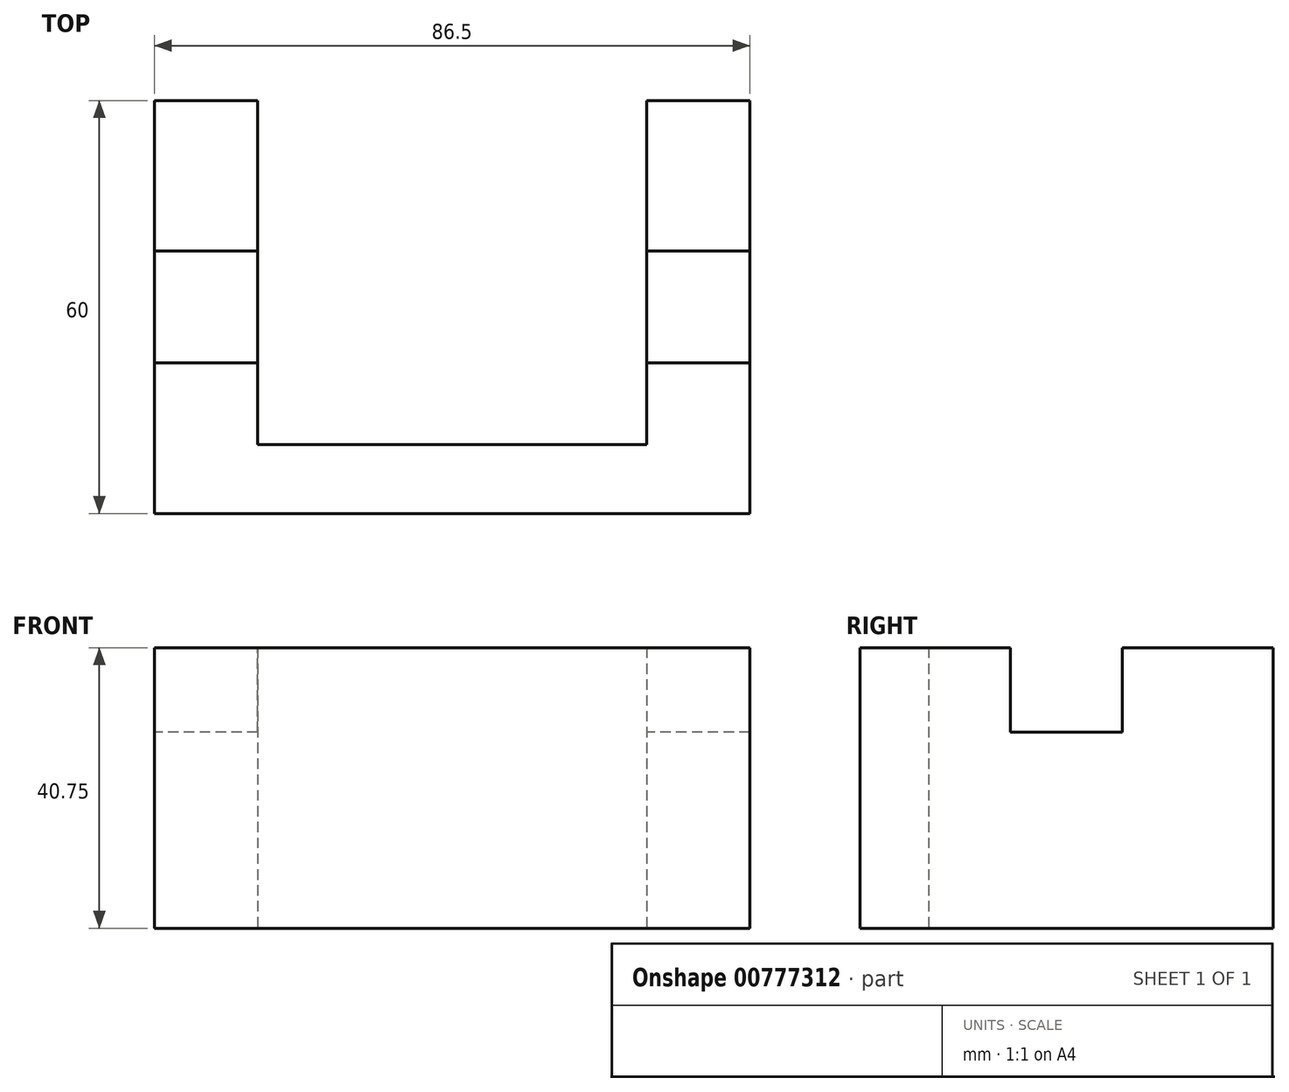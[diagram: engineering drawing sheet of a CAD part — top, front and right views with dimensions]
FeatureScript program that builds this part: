
annotation { "Feature Type Name" : "Feature", "Feature Type Description" : "" }
export const myFeature = defineFeature(function(context is Context, id is Id, definition is map)
    precondition{}
    {
        {
            var Q0;
            Q0=qCreatedBy(makeId("Top.planeOp"),FACE);
            var sketch = newSketch(context, id + "F0", { "sketchPlane" : qUnion([Q0])});
            skLineSegment(sketch, "E0.bottom", {"start": v(7.5, 30) * mm, "end": v(-7.5, 30) * mm});
            skLineSegment(sketch, "E0.top", {"start": v(7.5, -30) * mm, "end": v(-7.5, -30) * mm});
            skLineSegment(sketch, "E0.left", {"start": v(7.5, 30) * mm, "end": v(7.5, -30) * mm});
            skLineSegment(sketch, "E0.right", {"start": v(-7.5, 30) * mm, "end": v(-7.5, -30) * mm});
            skPoint(sketch, "E0.middle", {"position": v(0, 0) * mm});
            skSolve(sketch);
        }
        {
            var Q0;
            Q0 = qSketchRegion(id + "F0", true);
            extrude(context, id + "F1", {"entities" : qUnion([Q0]), "depth" : 28.5 * mm, "offsetDistance" : 25 * mm});
        }
        {
            var Q0;
            Q0=makeQuery(id+"F1.opExtrude","CAP_FACE",FACE,{"disambiguationData":[OSD([sQuery(id+"F0.wireOp",EDGE,"E0.bottom"),sQuery(id+"F0.wireOp",EDGE,"E0.top"),sQuery(id+"F0.wireOp",EDGE,"E0.left"),sQuery(id+"F0.wireOp",EDGE,"E0.right")])],"isStart":false});
            var sketch = newSketch(context, id + "F2", { "sketchPlane" : qUnion([Q0])});
            skLineSegment(sketch, "E1.bottom", {"start": v(7.5, 8.12) * mm, "end": v(-7.5, 8.12) * mm});
            skLineSegment(sketch, "E1.top", {"start": v(7.5, -8.12) * mm, "end": v(-7.5, -8.12) * mm});
            skLineSegment(sketch, "E1.left", {"start": v(7.5, 8.12) * mm, "end": v(7.5, -8.12) * mm});
            skLineSegment(sketch, "E1.right", {"start": v(-7.5, 8.12) * mm, "end": v(-7.5, -8.12) * mm});
            skPoint(sketch, "E1.middle", {"position": v(0, 0) * mm});
            skSolve(sketch);
        }
        {
            var Q0;
            {var subQ0=sQuery(id+"F0.wireOp",EDGE,"E0.left");Q0=makeQuery(id+"F411Q4QD505CHMR_1.boolean.opBoolean","MERGE",FACE,{"derivedFrom":[makeQuery(id+"F1.opExtrude","CAP_FACE",FACE,{"disambiguationData":[OSD([sQuery(id+"F0.wireOp",EDGE,"E0.bottom"),sQuery(id+"F0.wireOp",EDGE,"E0.top"),subQ0,sQuery(id+"F0.wireOp",EDGE,"E0.right")])],"isStart":true}),makeQuery(id+"F411Q4QD505CHMR_1.opExtrude","SWEPT_FACE",FACE,{"disambiguationData":[OSD([subQ0]),TDD([makeQuery(id+"F1.opExtrude","CAP_EDGE",EDGE,{"disambiguationData":[OSD([subQ0])],"isStart":true})])]})]});}
            var sketch = newSketch(context, id + "F3", { "sketchPlane" : qUnion([Q0])});
            skLineSegment(sketch, "E2.bottom", {"start": v(7.5, 20) * mm, "end": v(64, 20) * mm});
            skLineSegment(sketch, "E2.top", {"start": v(7.5, -30) * mm, "end": v(64, -30) * mm});
            skLineSegment(sketch, "E2.left", {"start": v(7.5, 20) * mm, "end": v(7.5, -30) * mm});
            skLineSegment(sketch, "E2.right", {"start": v(64, 20) * mm, "end": v(64, -30) * mm});
            skSolve(sketch);
        }
        {
            var Q0;
            Q0=makeQuery(id+"F3.imprint","IMPRINT",FACE,{"disambiguationData":[TD([[makeQuery(id+"F3.imprint","IMPRINT",EDGE,{"derivedFrom":sQuery(id+"F3.wireOp",EDGE,"E2.bottom")}),-1.0]])]});
            extrude(context, id + "F4", {"entities" : qUnion([Q0]), "operationType" : NewBodyOperationType.REMOVE, "endBound" : BoundingType.THROUGH_ALL, "oppositeDirection" : true, "depth" : 25 * mm, "offsetDistance" : 25 * mm});
        }
        {
            var Q0;
            {var subQ0=sQuery(id+"F2.wireOp",EDGE,"E1.bottom");Q0=makeQuery(id+"F2.imprint","IMPRINT",FACE,{"disambiguationData":[TD([[makeQuery(id+"F2.imprint","IMPRINT",EDGE,{"derivedFrom":subQ0}),-1.0]])]});}
            var Q1;
            {var subQ0=sQuery(id+"F2.wireOp",EDGE,"E1.top");Q1=makeQuery(id+"F2.imprint","IMPRINT",FACE,{"disambiguationData":[TD([[makeQuery(id+"F2.imprint","IMPRINT",EDGE,{"derivedFrom":subQ0}),1.0]])]});}
            extrude(context, id + "F5", {"entities" : qUnion([Q0, Q1]), "operationType" : NewBodyOperationType.ADD, "depth" : 12.25 * mm, "offsetDistance" : 25 * mm});
        }
        {
            var Q0;
            {var subQ0=sQuery(id+"F0.wireOp",EDGE,"E0.left");var subQ1=makeQuery(id+"F1.opExtrude","CAP_EDGE",EDGE,{"disambiguationData":[OSD([subQ0])],"isStart":false});Q0=makeQuery(id+"F5.boolean.opBoolean","MERGE",FACE,{"derivedFrom":[makeQuery(id+"F1.opExtrude","SWEPT_FACE",FACE,{"disambiguationData":[OSD([subQ0])]}),makeQuery(id+"F5.opExtrude","SWEPT_FACE",FACE,{"disambiguationData":[OSD([subQ0]),TDD([makeQuery(id+"F2.imprint","IMPRINT",EDGE,{"disambiguationData":[TD([[makeQuery(id+"F2.imprint","INTERSECT",VERTEX,{"derivedFrom":[makeQuery(id+"F1.opExtrude","CAP_EDGE",EDGE,{"disambiguationData":[OSD([sQuery(id+"F0.wireOp",EDGE,"E0.bottom")])],"isStart":false}),subQ1]}),-1.0]])],"derivedFrom":subQ1})])]}),makeQuery(id+"F5.opExtrude","SWEPT_FACE",FACE,{"disambiguationData":[OSD([subQ0]),TDD([makeQuery(id+"F2.imprint","IMPRINT",EDGE,{"disambiguationData":[TD([[makeQuery(id+"F2.imprint","INTERSECT",VERTEX,{"derivedFrom":[makeQuery(id+"F1.opExtrude","CAP_EDGE",EDGE,{"disambiguationData":[OSD([sQuery(id+"F0.wireOp",EDGE,"E0.top")])],"isStart":false}),subQ1]}),1.0]])],"derivedFrom":subQ1})])]})]});}
            extrude(context, id + "F6", {"entities" : qUnion([Q0]), "operationType" : NewBodyOperationType.ADD, "depth" : 71.5 * mm, "offsetDistance" : 25 * mm});
        }
        {
            var Q0;
            Q0 = qSketchRegion(id + "F3", true);
            extrude(context, id + "F7", {"entities" : qUnion([Q0]), "operationType" : NewBodyOperationType.REMOVE, "endBound" : BoundingType.THROUGH_ALL, "oppositeDirection" : true, "depth" : 25 * mm, "offsetDistance" : 25 * mm});
        }
    });
